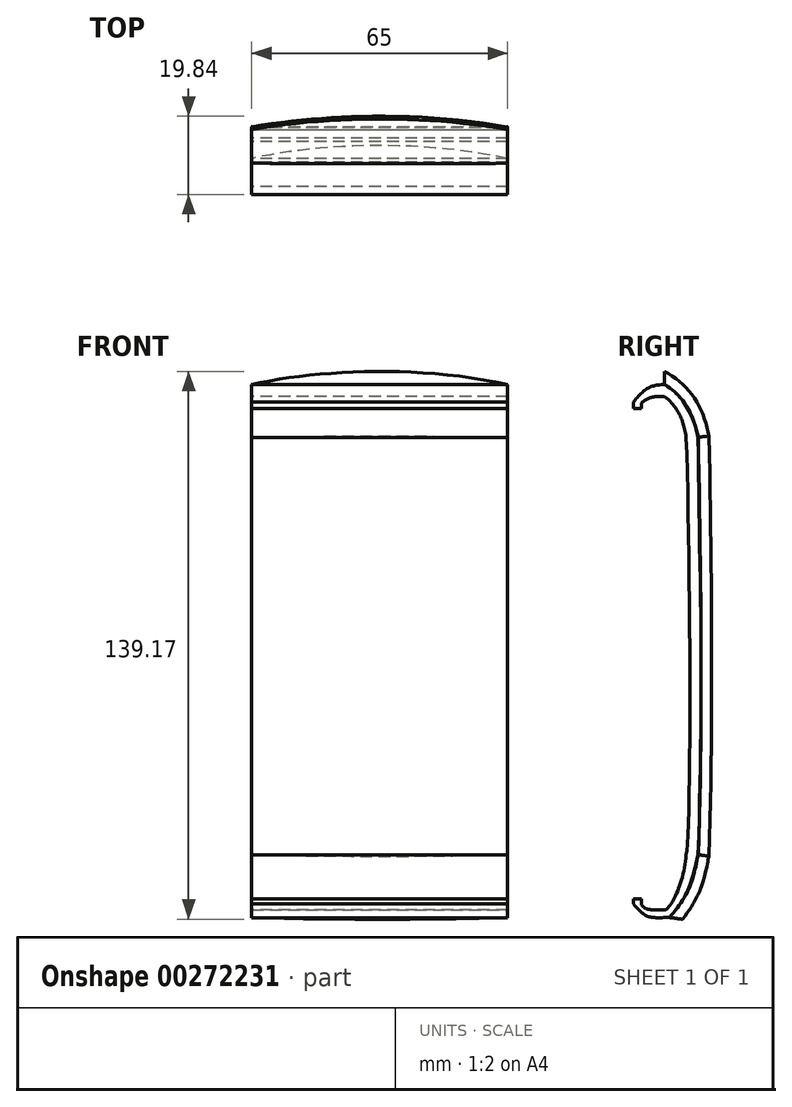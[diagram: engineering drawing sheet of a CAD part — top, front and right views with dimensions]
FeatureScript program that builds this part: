
annotation { "Feature Type Name" : "Feature", "Feature Type Description" : "" }
export const myFeature = defineFeature(function(context is Context, id is Id, definition is map)
    precondition{}
    {
        {
            var Q0;
            Q0=qCreatedBy(makeId("Right.planeOp"),FACE);
            var sketch = newSketch(context, id + "F0", { "sketchPlane" : qUnion([Q0])});
            skLineSegment(sketch, "E0", {"start": v(18.77, 0) * mm, "end": v(18.77, 127.25) * mm});
            skFitSpline(sketch, "E1", {"points": [v(18.77, 127.25) * mm, v(24.67, 128.91) * mm], "startDerivative": vector(6.09, 5.47) * mm, "endDerivative": vector(6.78, -0.14) * mm});
            skFitSpline(sketch, "E2", {"points": [v(24.67, 128.91) * mm, v(30.13, 118.56) * mm], "startDerivative": vector(11.07, -9.13) * mm, "endDerivative": vector(1.94, -12.59) * mm});
            skFitSpline(sketch, "E3", {"points": [v(30.13, 118.56) * mm, v(30.13, 12.5) * mm], "startDerivative": vector(3.44, -92.69) * mm, "endDerivative": vector(-4, -14.9) * mm});
            skFitSpline(sketch, "E4", {"points": [v(30.13, 12.5) * mm, v(24.95, -1.48) * mm], "startDerivative": vector(-1.72, -19.62) * mm, "endDerivative": vector(-6.23, -4.45) * mm});
            skFitSpline(sketch, "E5", {"points": [v(18.77, 0) * mm, v(24.95, -1.48) * mm], "startDerivative": vector(1.26, -4.73) * mm, "endDerivative": vector(12.1, 0.27) * mm});
            skLineSegment(sketch, "E6", {"start": v(18.77, 127.25) * mm, "end": v(18.77, 125.83) * mm});
            skLineSegment(sketch, "E7", {"start": v(18.77, 125.83) * mm, "end": v(16.77, 125.83) * mm});
            skLineSegment(sketch, "E8", {"start": v(16.77, 125.83) * mm, "end": v(16.77, 127.53) * mm});
            skFitSpline(sketch, "E9", {"points": [v(16.77, 127.53) * mm, v(24.67, 131.91) * mm], "startDerivative": vector(7.62, 9.96) * mm, "endDerivative": vector(10.35, -0.34) * mm});
            skFitSpline(sketch, "E10", {"points": [v(24.67, 131.91) * mm, v(33.13, 118.56) * mm], "startDerivative": vector(16.3, -8.71) * mm, "endDerivative": vector(2.15, -11.45) * mm});
            skFitSpline(sketch, "E11", {"points": [v(33.13, 118.56) * mm, v(33.13, 12.5) * mm], "startDerivative": vector(1.4, -106.45) * mm, "endDerivative": vector(-4.64, -112.14) * mm});
            skFitSpline(sketch, "E12", {"points": [v(33.13, 12.5) * mm, v(25.82, -3.45) * mm], "startDerivative": vector(-5.57, -28.04) * mm, "endDerivative": vector(-10.94, -12.34) * mm});
            skFitSpline(sketch, "E13", {"points": [v(25.82, -3.45) * mm, v(16.77, 0) * mm], "startDerivative": vector(-16.37, -0.37) * mm, "endDerivative": vector(-9.81, 11.33) * mm});
            skLineSegment(sketch, "E14", {"start": v(16.77, 0) * mm, "end": v(16.77, 1.23) * mm});
            skLineSegment(sketch, "E15", {"start": v(16.77, 1.23) * mm, "end": v(18.77, 1.23) * mm});
            skSolve(sketch);
        }
        {
            var Q0;
            Q0=makeQuery(id+"F0.imprint","IMPRINT",FACE,{"disambiguationData":[TD([[makeQuery(id+"F0.imprint","IMPRINT",EDGE,{"derivedFrom":sQuery(id+"F0.wireOp",EDGE,"E1")}),1.0]])]});
            extrude(context, id + "F1", {"entities" : qUnion([Q0]), "depth" : 65 * mm});
        }
        {
            var Q0;
            Q0=qCreatedBy(makeId("Right.planeOp"),FACE);
            var sketch = newSketch(context, id + "F2", { "sketchPlane" : qUnion([Q0])});
            skFitSpline(sketch, "E16", {"points": [v(25.82, -3.45) * mm, v(33.13, 12.5) * mm], "startDerivative": vector(15.55, 17.4) * mm, "endDerivative": vector(3.46, 17.25) * mm});
            skFitSpline(sketch, "E17", {"points": [v(33.13, 118.56) * mm, v(33.13, 12.5) * mm], "startDerivative": vector(2.35, -104.9) * mm, "endDerivative": vector(-3.16, -102.1) * mm});
            skFitSpline(sketch, "E18", {"points": [v(33.13, 118.56) * mm, v(24.67, 131.91) * mm], "startDerivative": vector(-4.67, 21.76) * mm, "endDerivative": vector(-11.87, 7.75) * mm});
            skSolve(sketch);
        }
        {
            var Q0;
            Q0=qCreatedBy(makeId("Top.planeOp"),FACE);
            var sketch = newSketch(context, id + "F3", { "sketchPlane" : qUnion([Q0])});
            skLineSegment(sketch, "E19", {"start": v(65, 28.62) * mm, "end": v(0, 28.62) * mm});
            skFitSpline(sketch, "E20", {"points": [v(65, 28.62) * mm, v(0, 28.62) * mm], "startDerivative": vector(-70.3, 15.07) * mm, "endDerivative": vector(-51.08, -11.05) * mm});
            skSolve(sketch);
        }
        {
            var Q0;
            Q0 = qSketchRegion(id + "F3", true);
            var Q1;
            Q1 = qConstructionFilter(qBodyType(qCreatedBy(id + "F2" ,EDGE), BodyType.WIRE), ConstructionObject.NO);
            sweep(context, id + "F4", {"profiles" : qUnion([Q0]), "path" : qUnion([Q1])});
        }
    });
